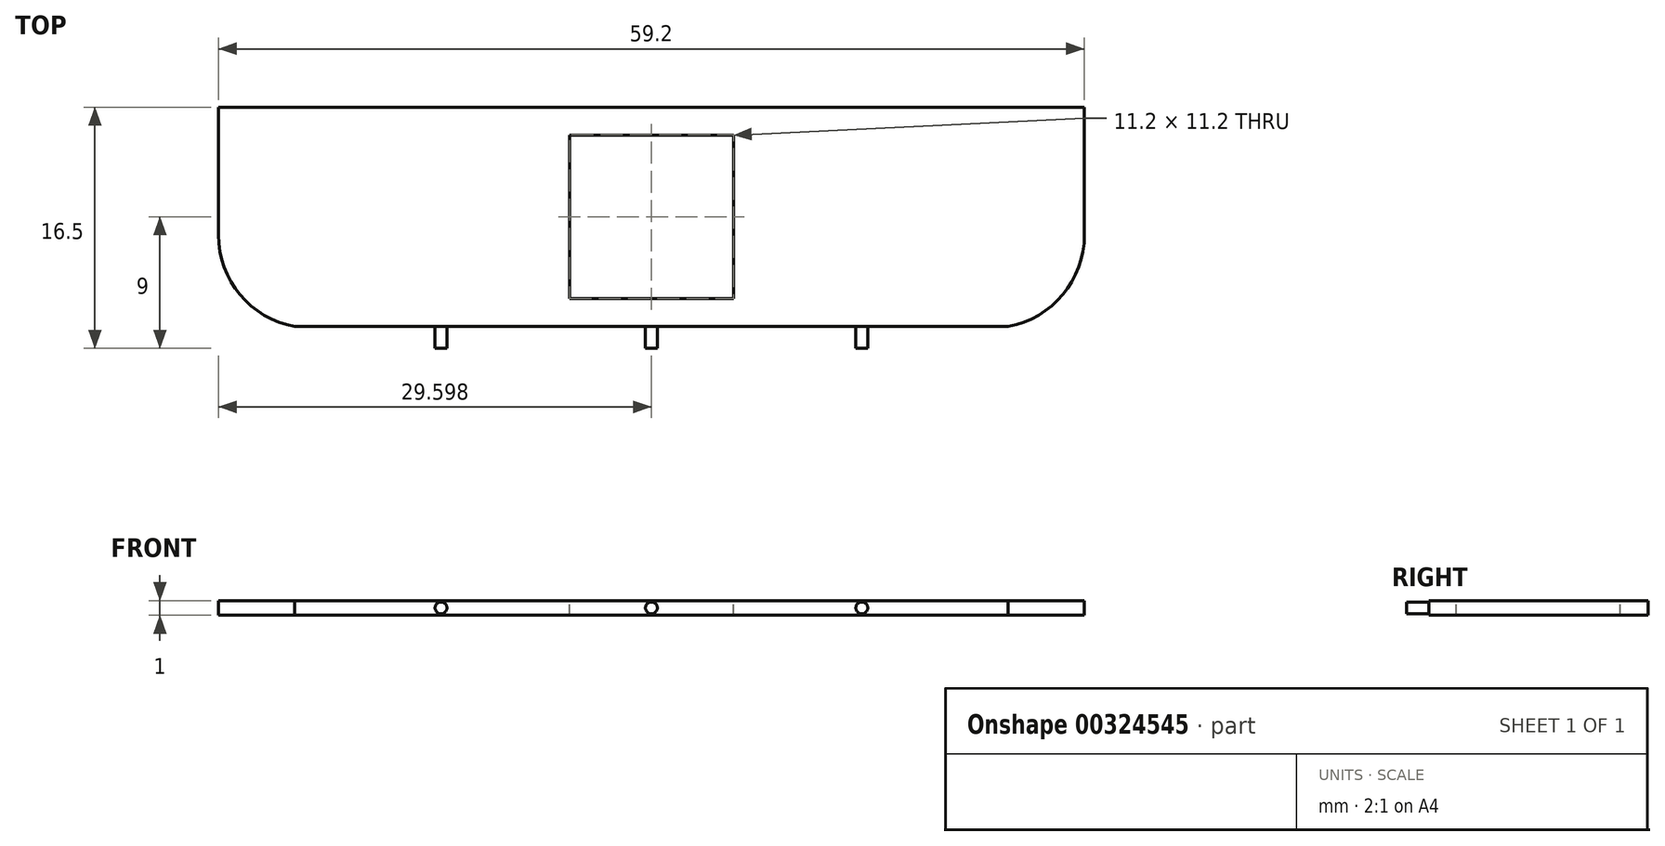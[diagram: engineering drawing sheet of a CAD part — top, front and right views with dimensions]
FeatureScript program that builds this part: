
annotation { "Feature Type Name" : "Feature", "Feature Type Description" : "" }
export const myFeature = defineFeature(function(context is Context, id is Id, definition is map)
    precondition{}
    {
        {
            var Q0;
            Q0=qCreatedBy(makeId("Top.planeOp"),FACE);
            var sketch = newSketch(context, id + "F0", { "sketchPlane" : qUnion([Q0])});
            skLineSegment(sketch, "E0", {"start": v(-29.01, 0) * mm, "end": v(19.75, 0) * mm});
            skPoint(sketch, "E1.visualSharp", {"position": v(-34.23, 0) * mm});
            skArc(sketch, "E1.filletArc", {"start": v(-34.23, 6.25) * mm, "mid": v(-32.76, 2.18) * mm, "end": v(-29.01, 0) * mm});
            skArc(sketch, "E2.MirrorCS", {"start": v(24.97, 6.25) * mm, "mid": v(23.5, 2.18) * mm, "end": v(19.75, 0) * mm});
            skLineSegment(sketch, "E3.top", {"start": v(-34.23, 15) * mm, "end": v(24.97, 15) * mm});
            skLineSegment(sketch, "E3.left", {"start": v(-34.23, 6.25) * mm, "end": v(-34.23, 15) * mm});
            skLineSegment(sketch, "E3.right", {"start": v(24.97, 6.25) * mm, "end": v(24.97, 15) * mm});
            skSolve(sketch);
        }
        {
            var Q0;
            Q0 = qSketchRegion(id + "F0", true);
            extrude(context, id + "F1", {"entities" : qUnion([Q0]), "oppositeDirection" : true, "depth" : 1 * mm});
        }
        {
            var Q0;
            Q0=makeQuery(id+"F1.opExtrude","SWEPT_FACE",FACE,{"disambiguationData":[OSD([sQuery(id+"F0.wireOp",EDGE,"E0")])]});
            var sketch = newSketch(context, id + "F2", { "sketchPlane" : qUnion([Q0])});
            skLineSegment(sketch, "E4", {"start": v(-4.63, -1) * mm, "end": v(-4.63, 0) * mm, "construction": true});
            skPoint(sketch, "E4.endSnap0", {"position": v(-4.63, 0) * mm});
            skSolve(sketch);
        }
        {
            var Q0;
            {var subQ0=sQuery(id+"F0.wireOp",EDGE,"E0");Q0=makeQuery(id+"F2.imprint","IMPRINT",FACE,{"disambiguationData":[TD([[makeQuery(id+"F2.imprint","IMPRINT",EDGE,{"derivedFrom":makeQuery(id+"F1.opExtrude","CAP_EDGE",EDGE,{"disambiguationData":[OSD([subQ0])],"isStart":true})}),-1.0]])]});}
            var sketch = newSketch(context, id + "F3", { "sketchPlane" : qUnion([Q0])});
            skCircle(sketch, "E5", {"center": v(-19.01, -0.5) * mm, "radius": 0.4 * mm});
            skCircle(sketch, "E6", {"center": v(-4.63, -0.5) * mm, "radius": 0.4 * mm});
            skCircle(sketch, "E7", {"center": v(9.75, -0.5) * mm, "radius": 0.4 * mm});
            skSolve(sketch);
        }
        {
            var Q0;
            Q0 = qSketchRegion(id + "F3", true);
            extrude(context, id + "F4", {"entities" : qUnion([Q0]), "operationType" : NewBodyOperationType.ADD, "depth" : 1.5 * mm});
        }
        {
            var Q0;
            Q0=makeQuery(id+"F1.opExtrude","CAP_FACE",FACE,{"disambiguationData":[OSD([sQuery(id+"F0.wireOp",EDGE,"E0"),sQuery(id+"F0.wireOp",EDGE,"E1.filletArc"),sQuery(id+"F0.wireOp",EDGE,"E2.MirrorCS"),sQuery(id+"F0.wireOp",EDGE,"E3.top"),sQuery(id+"F0.wireOp",EDGE,"E3.left"),sQuery(id+"F0.wireOp",EDGE,"E3.right")])],"isStart":true});
            var sketch = newSketch(context, id + "F5", { "sketchPlane" : qUnion([Q0])});
            skLineSegment(sketch, "E8.bottom", {"start": v(-10.23, 13.1) * mm, "end": v(0.97, 13.1) * mm});
            skLineSegment(sketch, "E8.top", {"start": v(-10.23, 1.9) * mm, "end": v(0.97, 1.9) * mm});
            skLineSegment(sketch, "E8.left", {"start": v(-10.23, 13.1) * mm, "end": v(-10.23, 1.9) * mm});
            skLineSegment(sketch, "E8.right", {"start": v(0.97, 13.1) * mm, "end": v(0.97, 1.9) * mm});
            skSolve(sketch);
        }
        {
            var Q0;
            Q0=makeQuery(id+"F5.imprint","IMPRINT",FACE,{"disambiguationData":[TD([[makeQuery(id+"F5.imprint","IMPRINT",EDGE,{"derivedFrom":sQuery(id+"F5.wireOp",EDGE,"E8.bottom")}),-1.0]])]});
            extrude(context, id + "F6", {"entities" : qUnion([Q0]), "operationType" : NewBodyOperationType.REMOVE, "oppositeDirection" : true, "depth" : 1 * mm});
        }
    });
